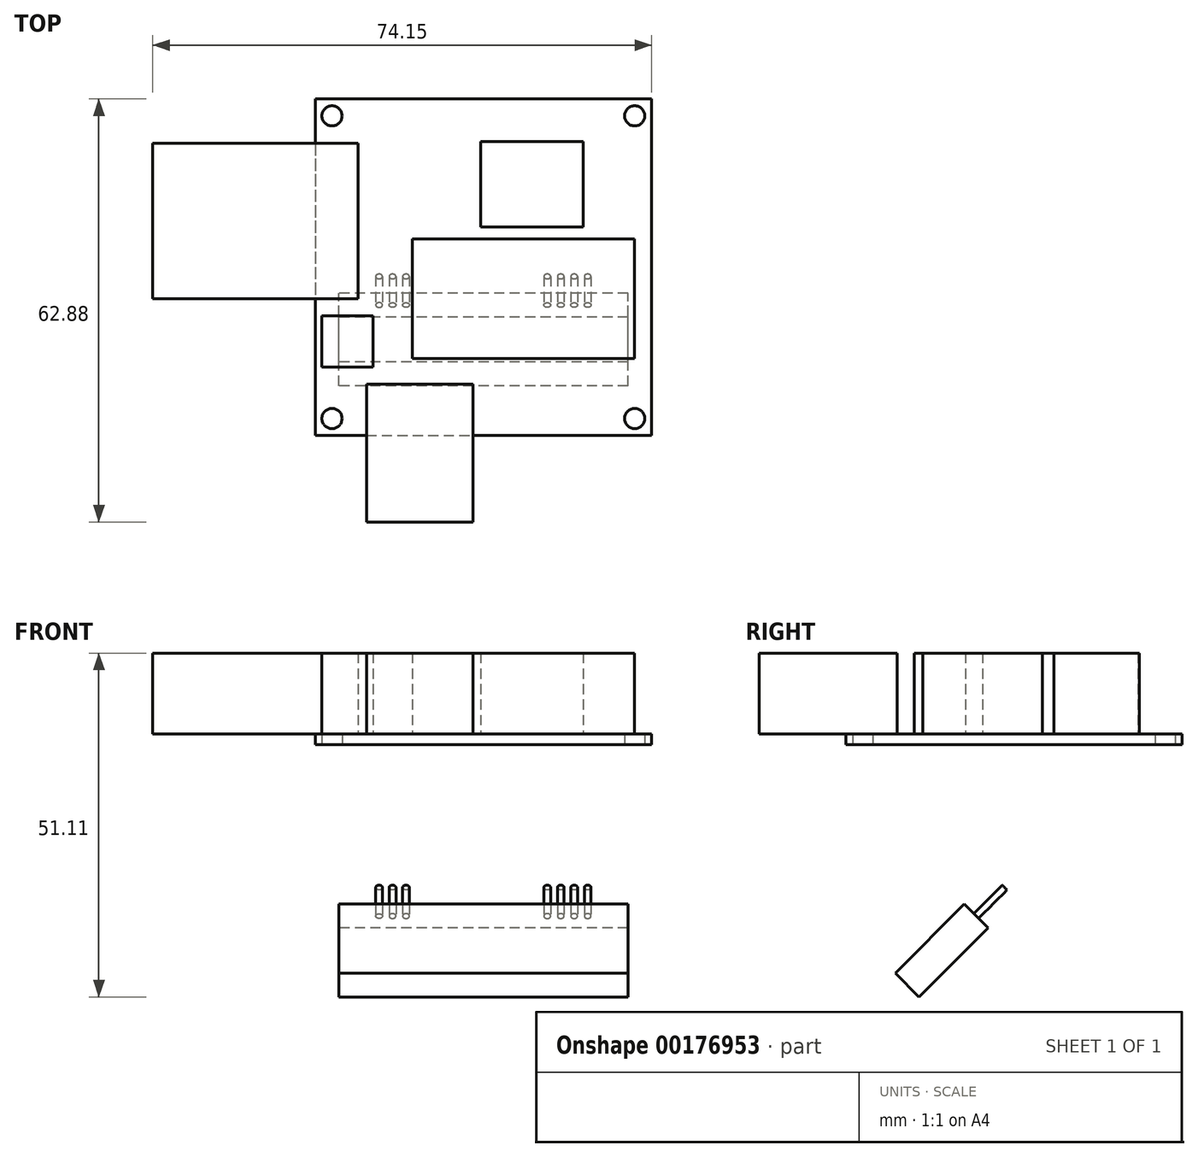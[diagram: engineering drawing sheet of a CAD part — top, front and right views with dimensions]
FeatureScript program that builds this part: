
annotation { "Feature Type Name" : "Feature", "Feature Type Description" : "" }
export const myFeature = defineFeature(function(context is Context, id is Id, definition is map)
    precondition{}
    {
        {
            var Q0;
            Q0=qCreatedBy(makeId("Top.planeOp"),FACE);
            var sketch = newSketch(context, id + "F0", { "sketchPlane" : qUnion([Q0])});
            skLineSegment(sketch, "E0.bottom", {"start": v(-25, 25) * mm, "end": v(25, 25) * mm});
            skLineSegment(sketch, "E0.top", {"start": v(-25, -25) * mm, "end": v(25, -25) * mm});
            skLineSegment(sketch, "E0.left", {"start": v(-25, 25) * mm, "end": v(-25, -25) * mm});
            skLineSegment(sketch, "E0.right", {"start": v(25, 25) * mm, "end": v(25, -25) * mm});
            skPoint(sketch, "E0.middle", {"position": v(0, 0) * mm});
            skCircle(sketch, "E1", {"center": v(-22.5, 22.5) * mm, "radius": 1.5 * mm});
            skCircle(sketch, "E2.MirrorC", {"center": v(22.5, 22.5) * mm, "radius": 1.5 * mm});
            skCircle(sketch, "E3.MirrorC", {"center": v(-22.5, -22.5) * mm, "radius": 1.5 * mm});
            skCircle(sketch, "E4.MirrorC", {"center": v(22.5, -22.5) * mm, "radius": 1.5 * mm});
            skSolve(sketch);
        }
        {
            var Q0;
            Q0=makeQuery(id+"F0.imprint","IMPRINT",FACE,{"disambiguationData":[TD([[makeQuery(id+"F0.imprint","IMPRINT",EDGE,{"derivedFrom":sQuery(id+"F0.wireOp",EDGE,"E0.bottom")}),-1.0]])]});
            extrude(context, id + "F1", {"entities" : qUnion([Q0]), "depth" : 1.6 * mm});
        }
        {
            var Q0;
            Q0=makeQuery(id+"F1.opExtrude","CAP_FACE",FACE,{"disambiguationData":[OSD([sQuery(id+"F0.wireOp",EDGE,"E0.bottom"),sQuery(id+"F0.wireOp",EDGE,"E0.top"),sQuery(id+"F0.wireOp",EDGE,"E0.left"),sQuery(id+"F0.wireOp",EDGE,"E0.right"),sQuery(id+"F0.wireOp",EDGE,"E1"),sQuery(id+"F0.wireOp",EDGE,"E2.MirrorC"),sQuery(id+"F0.wireOp",EDGE,"E3.MirrorC"),sQuery(id+"F0.wireOp",EDGE,"E4.MirrorC")])],"isStart":false});
            var sketch = newSketch(context, id + "F2", { "sketchPlane" : qUnion([Q0])});
            skLineSegment(sketch, "E5.bottom", {"start": v(22.46, -13.57) * mm, "end": v(-10.56, -13.57) * mm});
            skLineSegment(sketch, "E5.top", {"start": v(22.46, 4.21) * mm, "end": v(-10.56, 4.2) * mm});
            skLineSegment(sketch, "E5.left", {"start": v(22.46, -13.57) * mm, "end": v(22.46, 4.21) * mm});
            skLineSegment(sketch, "E5.right", {"start": v(-10.56, -13.57) * mm, "end": v(-10.56, 4.2) * mm});
            skPoint(sketch, "E5.middle", {"position": v(5.95, -4.68) * mm});
            skLineSegment(sketch, "E6.bottom", {"start": v(14.84, 5.95) * mm, "end": v(-0.4, 5.95) * mm});
            skLineSegment(sketch, "E6.top", {"start": v(14.84, 18.65) * mm, "end": v(-0.4, 18.65) * mm});
            skLineSegment(sketch, "E6.left", {"start": v(14.84, 5.95) * mm, "end": v(14.84, 18.65) * mm});
            skLineSegment(sketch, "E6.right", {"start": v(-0.4, 5.95) * mm, "end": v(-0.4, 18.65) * mm});
            skPoint(sketch, "E6.middle", {"position": v(7.22, 12.3) * mm});
            skLineSegment(sketch, "E7.bottom", {"start": v(-18.65, 18.42) * mm, "end": v(-49.15, 18.42) * mm});
            skLineSegment(sketch, "E7.top", {"start": v(-18.65, -4.68) * mm, "end": v(-49.15, -4.68) * mm});
            skLineSegment(sketch, "E7.left", {"start": v(-18.65, 18.42) * mm, "end": v(-18.65, -4.68) * mm});
            skLineSegment(sketch, "E7.right", {"start": v(-49.15, 18.42) * mm, "end": v(-49.15, -4.68) * mm});
            skLineSegment(sketch, "E8.bottom", {"start": v(-24, -7.22) * mm, "end": v(-16.38, -7.22) * mm});
            skLineSegment(sketch, "E8.top", {"start": v(-24, -14.84) * mm, "end": v(-16.38, -14.84) * mm});
            skLineSegment(sketch, "E8.left", {"start": v(-24, -7.22) * mm, "end": v(-24, -14.84) * mm});
            skLineSegment(sketch, "E8.right", {"start": v(-16.38, -7.22) * mm, "end": v(-16.38, -14.84) * mm});
            skLineSegment(sketch, "E9.bottom", {"start": v(-17.38, -17.38) * mm, "end": v(-1.52, -17.38) * mm});
            skLineSegment(sketch, "E9.top", {"start": v(-17.38, -37.88) * mm, "end": v(-1.52, -37.88) * mm});
            skLineSegment(sketch, "E9.left", {"start": v(-17.38, -17.38) * mm, "end": v(-17.38, -37.88) * mm});
            skLineSegment(sketch, "E9.right", {"start": v(-1.52, -17.38) * mm, "end": v(-1.52, -37.88) * mm});
            skLineSegment(sketch, "E10", {"start": v(-25, -25) * mm, "end": v(25, -25) * mm, "construction": true});
            skSolve(sketch);
        }
        {
            var Q0;
            Q0=makeQuery(id+"F2.imprint","IMPRINT",FACE,{"disambiguationData":[TD([[makeQuery(id+"F2.imprint","IMPRINT",EDGE,{"derivedFrom":sQuery(id+"F2.wireOp",EDGE,"E5.bottom")}),-1.0]])]});
            var Q1;
            Q1=makeQuery(id+"F2.imprint","IMPRINT",FACE,{"disambiguationData":[TD([[makeQuery(id+"F2.imprint","IMPRINT",EDGE,{"derivedFrom":sQuery(id+"F2.wireOp",EDGE,"E6.bottom")}),-1.0]])]});
            var Q2;
            {var subQ0=sQuery(id+"F2.wireOp",EDGE,"E7.left");Q2=makeQuery(id+"F2.imprint","IMPRINT",FACE,{"disambiguationData":[TD([[makeQuery(id+"F2.imprint","IMPRINT",EDGE,{"derivedFrom":subQ0}),-1.0]])]});}
            var Q3;
            {var subQ0=sQuery(id+"F2.wireOp",EDGE,"E7.right");Q3=makeQuery(id+"F2.imprint","IMPRINT",FACE,{"disambiguationData":[TD([[makeQuery(id+"F2.imprint","IMPRINT",EDGE,{"derivedFrom":subQ0}),1.0]])]});}
            var Q4;
            Q4=makeQuery(id+"F2.imprint","IMPRINT",FACE,{"disambiguationData":[TD([[makeQuery(id+"F2.imprint","IMPRINT",EDGE,{"derivedFrom":sQuery(id+"F2.wireOp",EDGE,"E8.bottom")}),-1.0]])]});
            var Q5;
            {var subQ0=sQuery(id+"F2.wireOp",EDGE,"E9.top");Q5=makeQuery(id+"F2.imprint","IMPRINT",FACE,{"disambiguationData":[TD([[makeQuery(id+"F2.imprint","IMPRINT",EDGE,{"derivedFrom":subQ0}),1.0]])]});}
            var Q6;
            {var subQ0=sQuery(id+"F2.wireOp",EDGE,"E9.bottom");Q6=makeQuery(id+"F2.imprint","IMPRINT",FACE,{"disambiguationData":[TD([[makeQuery(id+"F2.imprint","IMPRINT",EDGE,{"derivedFrom":subQ0}),-1.0]])]});}
            extrude(context, id + "F3", {"entities" : qUnion([Q0, Q1, Q2, Q3, Q4, Q5, Q6]), "operationType" : NewBodyOperationType.ADD, "depth" : 12 * mm});
        }
        {
            var Q0;
            Q0=makeQuery(id+"F2.imprint","IMPRINT",FACE,{"disambiguationData":[TD([[makeQuery(id+"F2.imprint","IMPRINT",EDGE,{"derivedFrom":sQuery(id+"F2.wireOp",EDGE,"E5.bottom")}),1.0]])]});
            var Q1;
            Q1=makeQuery(id+"F1.opExtrude","CAP_EDGE",EDGE,{"disambiguationData":[OSD([sQuery(id+"F0.wireOp",EDGE,"E0.bottom")])],"isStart":false});
            cPlane(context, id + "F4", {"entities" : qUnion([Q0, Q1]), "cplaneType" : CPlaneType.LINE_ANGLE, "offset" : 25 * mm, "angle" : 45 * degree, "width" : 150 * mm, "height" : 150 * mm});
        }
        {
            var Q0;
            Q0=qCreatedBy(id+"F4.planeOp",FACE);
            var sketch = newSketch(context, id + "F5", { "sketchPlane" : qUnion([Q0])});
            skLineSegment(sketch, "E11.bottom", {"start": v(-21.5, -36.5) * mm, "end": v(21.5, -36.5) * mm});
            skLineSegment(sketch, "E11.top", {"start": v(-21.5, -22) * mm, "end": v(21.5, -22) * mm});
            skLineSegment(sketch, "E11.left", {"start": v(-21.5, -36.5) * mm, "end": v(-21.5, -22) * mm});
            skLineSegment(sketch, "E11.right", {"start": v(21.5, -36.5) * mm, "end": v(21.5, -22) * mm});
            skLineSegment(sketch, "E12", {"start": v(0, -20) * mm, "end": v(-25, -20) * mm, "construction": true});
            skSolve(sketch);
        }
        {
            var Q0;
            Q0=makeQuery(id+"F5.imprint","IMPRINT",FACE,{"disambiguationData":[TD([[makeQuery(id+"F5.imprint","IMPRINT",EDGE,{"derivedFrom":sQuery(id+"F5.wireOp",EDGE,"E11.bottom")}),1.0]])]});
            extrude(context, id + "F6", {"entities" : qUnion([Q0]), "oppositeDirection" : true, "depth" : 5 * mm});
        }
        {
            var Q0;
            Q0=makeQuery(id+"F6.opExtrude","SWEPT_FACE",FACE,{"disambiguationData":[OSD([sQuery(id+"F5.wireOp",EDGE,"E11.top")])]});
            var sketch = newSketch(context, id + "F7", { "sketchPlane" : qUnion([Q0])});
            skCircle(sketch, "E13", {"center": v(15.5, -14.05) * mm, "radius": 0.5 * mm});
            skPoint(sketch, "E13.centerSnap0", {"position": v(21.5, -14.05) * mm});
            skCircle(sketch, "E14.1.0.0", {"center": v(13.5, -14.05) * mm, "radius": 0.5 * mm});
            skCircle(sketch, "E14.2.0.0", {"center": v(11.5, -14.05) * mm, "radius": 0.5 * mm});
            skLineSegment(sketch, "E14.direction1", {"start": v(15.5, -14.05) * mm, "end": v(13.5, -14.05) * mm, "construction": true});
            skLineSegment(sketch, "E15", {"start": v(0, -11.55) * mm, "end": v(0, -16.55) * mm, "construction": true});
            skCircle(sketch, "E16.MirrorC", {"center": v(-15.5, -14.05) * mm, "radius": 0.5 * mm});
            skCircle(sketch, "E17.1.0.0", {"center": v(-13.5, -14.05) * mm, "radius": 0.5 * mm});
            skCircle(sketch, "E17.2.0.0", {"center": v(-11.5, -14.05) * mm, "radius": 0.5 * mm});
            skCircle(sketch, "E17.3.0.0", {"center": v(-9.5, -14.05) * mm, "radius": 0.5 * mm});
            skLineSegment(sketch, "E17.direction1", {"start": v(-15.5, -14.05) * mm, "end": v(-13.5, -14.05) * mm, "construction": true});
            skSolve(sketch);
        }
        {
            var Q0;
            Q0 = qSketchRegion(id + "F7", true);
            extrude(context, id + "F8", {"entities" : qUnion([Q0]), "operationType" : NewBodyOperationType.ADD, "depth" : 6 * mm});
        }
    });
